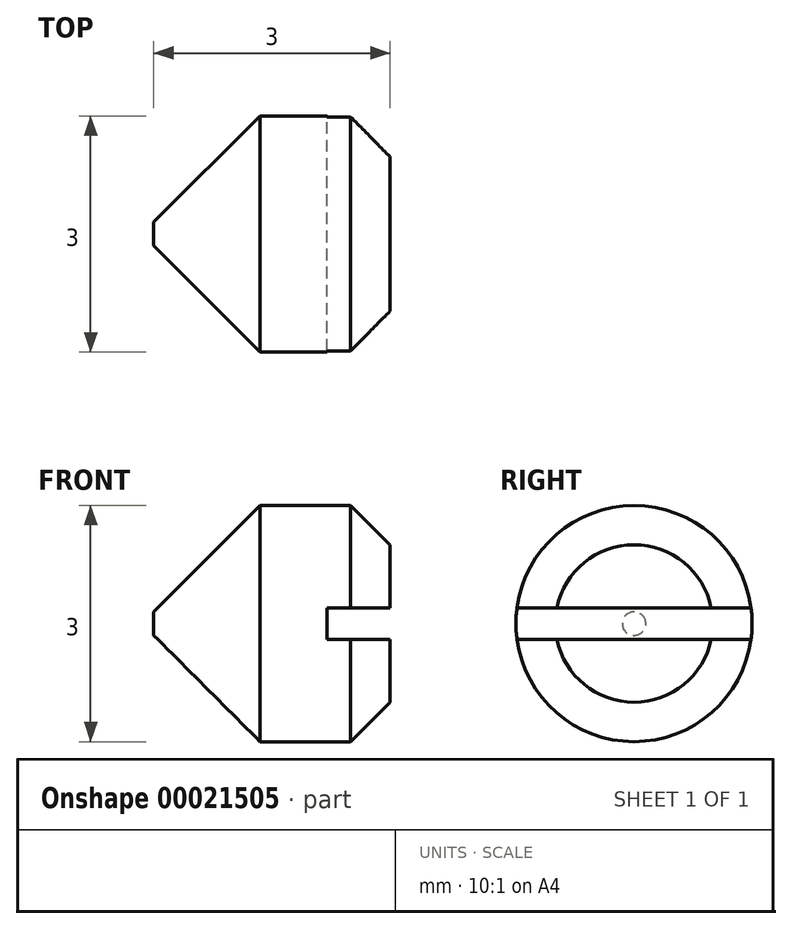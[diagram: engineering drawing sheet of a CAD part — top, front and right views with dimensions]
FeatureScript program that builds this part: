
annotation { "Feature Type Name" : "Feature", "Feature Type Description" : "" }
export const myFeature = defineFeature(function(context is Context, id is Id, definition is map)
    precondition{}
    {
        {
            var Q0;
            Q0=qCreatedBy(makeId("Front.planeOp"),FACE);
            var sketch = newSketch(context, id + "F2", { "sketchPlane" : qUnion([Q0])});
            skLineSegment(sketch, "E0", {"start": v(1.35, 1.5) * mm, "end": v(3, 1.5) * mm});
            skLineSegment(sketch, "E1", {"start": v(3, 1.5) * mm, "end": v(3, 0) * mm});
            skLineSegment(sketch, "E2", {"start": v(3, 0) * mm, "end": v(0, 0) * mm});
            skLineSegment(sketch, "E3", {"start": v(1.35, 1.5) * mm, "end": v(0, 0.15) * mm});
            skLineSegment(sketch, "E4", {"start": v(0, 0.15) * mm, "end": v(0, 0) * mm});
            skSolve(sketch);
        }
        {
            var Q0;
            Q0 = qSketchRegion(id + "F2", true);
            var Q1;
            Q1=sQuery(id+"F2.wireOp",EDGE,"E2");
            revolve(context, id + "F3", {"entities" : qUnion([Q0]), "axis" : qUnion([Q1]), "revolveType" : RevolveType.FULL});
        }
        {
            var Q0;
            Q0=makeQuery(id+"F3.opRevolve","SWEPT_FACE",FACE,{"disambiguationData":[OSD([sQuery(id+"F2.wireOp",EDGE,"E1")])]});
            var sketch = newSketch(context, id + "F0", { "sketchPlane" : qUnion([Q0])});
            skLineSegment(sketch, "E5.bottom", {"start": v(-1.5, 0.2) * mm, "end": v(1.5, 0.2) * mm});
            skLineSegment(sketch, "E5.top", {"start": v(-1.5, -0.2) * mm, "end": v(1.5, -0.2) * mm});
            skLineSegment(sketch, "E5.left", {"start": v(-1.5, 0.2) * mm, "end": v(-1.5, -0.2) * mm});
            skLineSegment(sketch, "E5.right", {"start": v(1.5, 0.2) * mm, "end": v(1.5, -0.2) * mm});
            skLineSegment(sketch, "E6", {"start": v(-1.5, 0) * mm, "end": v(1.5, 0) * mm, "construction": true});
            skSolve(sketch);
        }
        {
            var Q0;
            Q0=makeQuery(id+"F3.opRevolve","SWEPT_EDGE",EDGE,{"disambiguationData":[OSD([sQuery(id+"F2.wireOp",EDGE,"E0"),sQuery(id+"F2.wireOp",EDGE,"E1")])]});
            chamfer(context, id + "F1", {"entities" : qUnion([Q0]), "width" : 0.5 * mm, "tangentPropagation" : true});
        }
        {
            var Q0;
            Q0 = qSketchRegion(id + "F0", true);
            extrude(context, id + "F4", {"entities" : qUnion([Q0]), "operationType" : NewBodyOperationType.REMOVE, "oppositeDirection" : true, "depth" : 0.8 * mm});
        }
    });
